# Revit family: Locker_SalsburyInd_Metal-1-Tier-Triple
name_source: partatom
category: Specialty Equipment
units: mm (PartAtom-declared; Revit-internal decimal feet)

## family parameters
Always vertical = Yes
Cut with Voids When Loaded = No
Maintain Annotation Orientation = No
OmniClass Number = 23.40.00.00
OmniClass Title = Equipment and Furnishings
Part Type = Normal
Room Calculation Point = No
Round Connector Dimension = Use Diameter
Shared = No
Work Plane-Based = No

## types (1)
- Locker_SalsburyInd_Metal-1-Tier-Triple
    Assembly Code = C1030310
    Base Height = 0 "
    Base Type = ML_Base Type : No Legs
    Construction Details = http://www.arcat.com
    Default Elevation = 0 "
    Description = Salsbury Locker as Specified
    Door Height = 57.812 "
    Door Width = 9.874 "
    Expected Lifespan (Years) = 0
    Keynote = 10 50 00
    Maintenance Schedule (Months) = 0
    Manufacturer = Salsbury Industries
    Manufacturer Fax = 323-846-6800
    Manufacturer Website = http://www.lockers.com
    Model = as Specified
    Product Data = http://www.arcat.com
    Product Properties = http://www.lockers.com
    Revision = R1_2017-09
    Sales Information = http://www.lockers.com
    Type Comments = Specify Assembled or Disassembled
    URL = www.lockers.com
    Unit Depth = 12 "
    Unit Height = 60 "
    Unit Width = 12 "
    Warranty Duration (Years) = 0

## geometry (parser evidence)
native form markers: Sweep x16
no freeform markers — native parametric forms only
